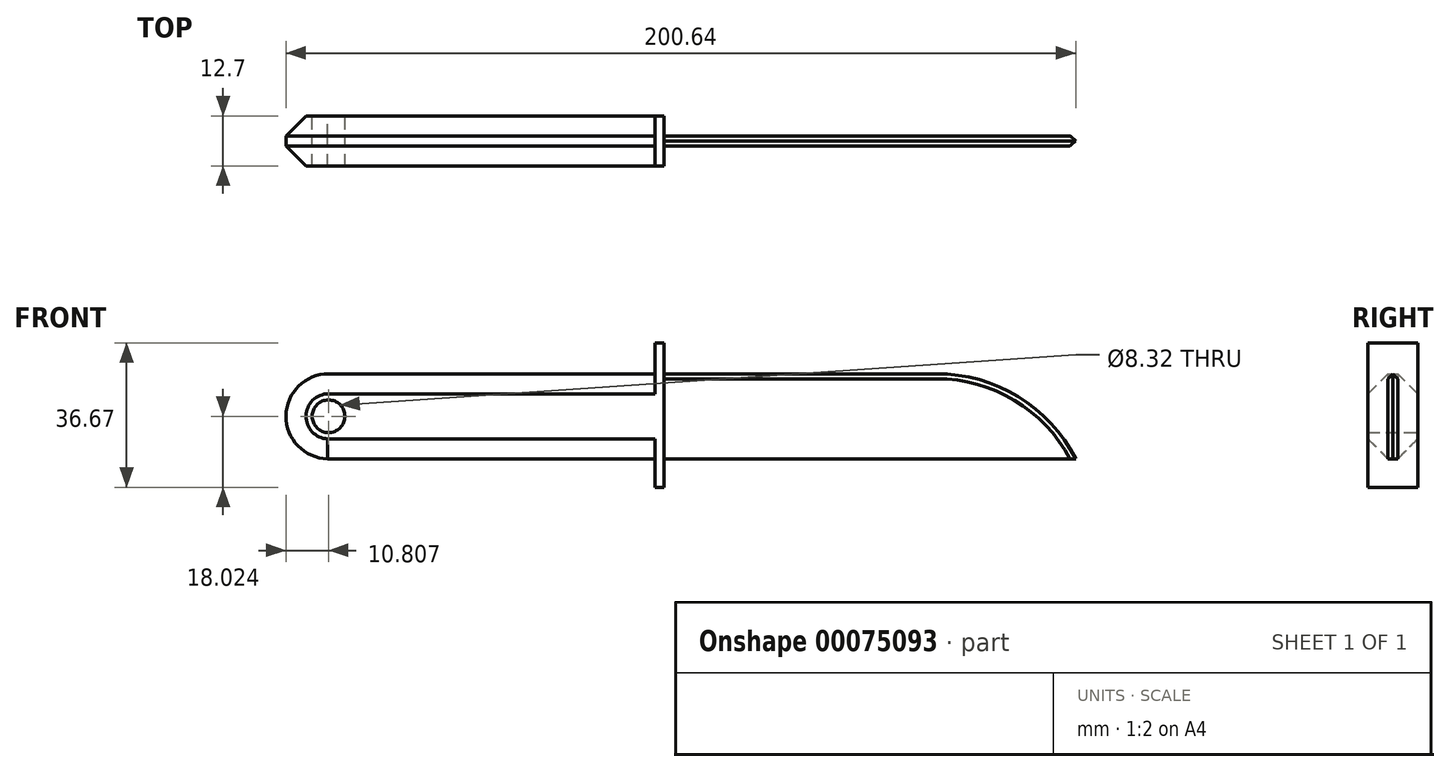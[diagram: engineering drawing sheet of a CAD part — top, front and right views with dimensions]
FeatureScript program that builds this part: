
annotation { "Feature Type Name" : "Feature", "Feature Type Description" : "" }
export const myFeature = defineFeature(function(context is Context, id is Id, definition is map)
    precondition{}
    {
        {
            var Q0;
            Q0=qCreatedBy(makeId("Front.planeOp"),FACE);
            var sketch = newSketch(context, id + "F0", { "sketchPlane" : qUnion([Q0])});
            skLineSegment(sketch, "E0", {"start": v(-30.61, 0) * mm, "end": v(52.65, 0) * mm});
            skLineSegment(sketch, "E1", {"start": v(-30.34, 21.61) * mm, "end": v(52.65, 21.61) * mm});
            skLineSegment(sketch, "E2", {"start": v(52.65, 21.61) * mm, "end": v(52.65, 29.45) * mm});
            skLineSegment(sketch, "E3", {"start": v(52.65, 29.45) * mm, "end": v(54.87, 29.45) * mm});
            skLineSegment(sketch, "E4", {"start": v(54.87, 29.45) * mm, "end": v(54.87, -7.22) * mm});
            skLineSegment(sketch, "E5", {"start": v(54.87, -7.22) * mm, "end": v(52.65, -7.22) * mm});
            skLineSegment(sketch, "E6", {"start": v(52.65, -7.22) * mm, "end": v(52.65, 0) * mm});
            skLineSegment(sketch, "E7", {"start": v(54.87, 0) * mm, "end": v(126.07, 0) * mm});
            skLineSegment(sketch, "E8", {"start": v(54.87, 21.61) * mm, "end": v(124.12, 21.61) * mm});
            skArc(sketch, "E9", {"start": v(159.49, 0) * mm, "mid": v(144.85, 15.78) * mm, "end": v(124.12, 21.61) * mm});
            skLineSegment(sketch, "E10", {"start": v(126.07, 0) * mm, "end": v(159.49, 0) * mm});
            skArc(sketch, "E11", {"start": v(-30.34, 21.61) * mm, "mid": v(-41.15, 10.94) * mm, "end": v(-30.61, 0) * mm});
            skCircle(sketch, "E12", {"center": v(-30.34, 10.8) * mm, "radius": 4.16 * mm});
            skSolve(sketch);
        }
        {
            var Q0;
            Q0=makeQuery(id+"F0.imprint","IMPRINT",FACE,{"disambiguationData":[TD([[makeQuery(id+"F0.imprint","IMPRINT",EDGE,{"derivedFrom":sQuery(id+"F0.wireOp",EDGE,"E0")}),1.0]])]});
            extrude(context, id + "F1", {"entities" : qUnion([Q0]), "depth" : 6.35 * mm});
        }
        {
            var Q0;
            Q0=makeQuery(id+"F1.opExtrude","CAP_FACE",FACE,{"disambiguationData":[OSD([sQuery(id+"F0.wireOp",EDGE,"E0"),sQuery(id+"F0.wireOp",EDGE,"xaIs6tCj-0HQ9-MyH3-FU1K-w0owBSLvuoZQ"),sQuery(id+"F0.wireOp",EDGE,"E1"),sQuery(id+"F0.wireOp",EDGE,"E2"),sQuery(id+"F0.wireOp",EDGE,"E3"),sQuery(id+"F0.wireOp",EDGE,"E4"),sQuery(id+"F0.wireOp",EDGE,"E5"),sQuery(id+"F0.wireOp",EDGE,"E6")])],"isStart":true});
            extrude(context, id + "F2", {"entities" : qUnion([Q0]), "operationType" : NewBodyOperationType.ADD, "depth" : 6.35 * mm});
        }
        {
            var Q0;
            {var subQ1=sQuery(id+"F0.wireOp",EDGE,"E7");Q0=makeQuery(id+"F0.imprint","IMPRINT",FACE,{"disambiguationData":[TD([[makeQuery(id+"F0.imprint","IMPRINT",EDGE,{"derivedFrom":subQ1}),1.0]])]});}
            extrude(context, id + "F3", {"entities" : qUnion([Q0]), "operationType" : NewBodyOperationType.ADD, "depth" : 1.27 * mm});
        }
        {
            var Q0;
            {var subQ1=sQuery(id+"F0.wireOp",EDGE,"E7");Q0=makeQuery(id+"F0.imprint","IMPRINT",FACE,{"disambiguationData":[TD([[makeQuery(id+"F0.imprint","IMPRINT",EDGE,{"derivedFrom":subQ1}),1.0]])]});}
            extrude(context, id + "F4", {"entities" : qUnion([Q0]), "operationType" : NewBodyOperationType.ADD, "oppositeDirection" : true, "depth" : 1.27 * mm});
        }
        {
            var Q0;
            Q0=makeQuery(id+"F1.opExtrude","CAP_EDGE",EDGE,{"disambiguationData":[OSD([sQuery(id+"F0.wireOp",EDGE,"E1")])],"isStart":false});
            var Q1;
            Q1=makeQuery(id+"F1.opExtrude","CAP_EDGE",EDGE,{"disambiguationData":[OSD([sQuery(id+"F0.wireOp",EDGE,"E0")])],"isStart":false});
            var Q2;
            Q2=makeQuery(id+"F2.opExtrude","CAP_EDGE",EDGE,{"disambiguationData":[OSD([sQuery(id+"F0.wireOp",EDGE,"E0")])],"isStart":false});
            var Q3;
            Q3=makeQuery(id+"F2.opExtrude","CAP_EDGE",EDGE,{"disambiguationData":[OSD([sQuery(id+"F0.wireOp",EDGE,"E1")])],"isStart":false});
            chamfer(context, id + "F5", {"entities" : qUnion([Q0, Q1, Q2, Q3]), "width" : 5.08 * mm, "tangentPropagation" : true});
        }
        {
            var Q0;
            Q0=makeQuery(id+"F3.opExtrude","CAP_EDGE",EDGE,{"disambiguationData":[OSD([sQuery(id+"F0.wireOp",EDGE,"E8")])],"isStart":false});
            var Q1;
            Q1=makeQuery(id+"F4.opExtrude","CAP_EDGE",EDGE,{"disambiguationData":[OSD([sQuery(id+"F0.wireOp",EDGE,"E8")])],"isStart":false});
            chamfer(context, id + "F6", {"entities" : qUnion([Q0, Q1]), "width" : 1.27 * mm, "tangentPropagation" : true});
        }
    });
